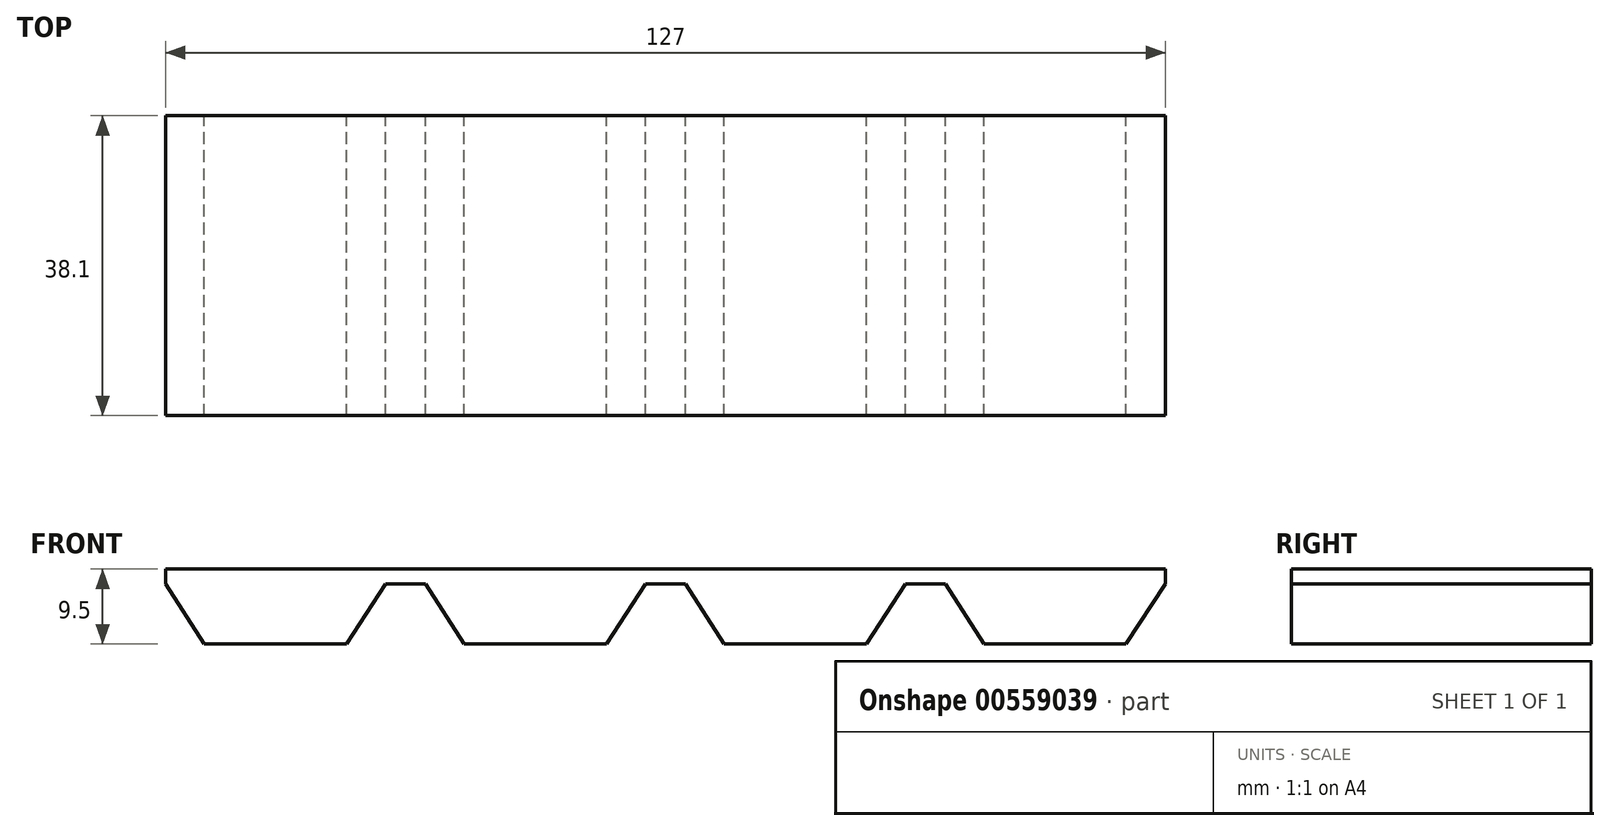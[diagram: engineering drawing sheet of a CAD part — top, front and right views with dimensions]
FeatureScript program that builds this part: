
annotation { "Feature Type Name" : "Feature", "Feature Type Description" : "" }
export const myFeature = defineFeature(function(context is Context, id is Id, definition is map)
    precondition{}
    {
        {
            var Q0;
            Q0=qCreatedBy(makeId("Front.planeOp"),FACE);
            var sketch = newSketch(context, id + "F0", { "sketchPlane" : qUnion([Q0])});
            skLineSegment(sketch, "E0", {"start": v(-63.5, 25.4) * mm, "end": v(63.5, 25.4) * mm});
            skLineSegment(sketch, "E1", {"start": v(-63.5, 25.4) * mm, "end": v(-58.6, 17.78) * mm});
            skLineSegment(sketch, "E2", {"start": v(-58.6, 17.78) * mm, "end": v(-40.55, 17.78) * mm});
            skLineSegment(sketch, "E3.MirrorCS", {"start": v(-35.56, 25.4) * mm, "end": v(-40.55, 17.78) * mm});
            skLineSegment(sketch, "E4.1.0.0", {"start": v(-2.54, 25.4) * mm, "end": v(-7.53, 17.78) * mm});
            skLineSegment(sketch, "E4.1.0.1", {"start": v(-25.58, 17.78) * mm, "end": v(-7.53, 17.78) * mm});
            skLineSegment(sketch, "E4.1.0.2", {"start": v(-30.48, 25.4) * mm, "end": v(-25.58, 17.78) * mm});
            skLineSegment(sketch, "E4.2.0.0", {"start": v(30.48, 25.4) * mm, "end": v(25.5, 17.78) * mm});
            skLineSegment(sketch, "E4.2.0.1", {"start": v(7.44, 17.78) * mm, "end": v(25.5, 17.78) * mm});
            skLineSegment(sketch, "E4.2.0.2", {"start": v(2.54, 25.4) * mm, "end": v(7.44, 17.78) * mm});
            skLineSegment(sketch, "E4.3.0.0", {"start": v(63.5, 25.4) * mm, "end": v(58.51, 17.78) * mm});
            skLineSegment(sketch, "E4.3.0.1", {"start": v(40.46, 17.78) * mm, "end": v(58.51, 17.78) * mm});
            skLineSegment(sketch, "E4.3.0.2", {"start": v(35.56, 25.4) * mm, "end": v(40.46, 17.78) * mm});
            skLineSegment(sketch, "E4.direction1", {"start": v(-58.6, 17.78) * mm, "end": v(-25.58, 17.78) * mm, "construction": true});
            skLineSegment(sketch, "E5", {"start": v(-63.5, 25.4) * mm, "end": v(-63.5, 27.28) * mm});
            skLineSegment(sketch, "E6", {"start": v(-63.5, 27.28) * mm, "end": v(63.48, 27.28) * mm});
            skLineSegment(sketch, "E7", {"start": v(63.48, 27.28) * mm, "end": v(63.5, 25.4) * mm});
            skSolve(sketch);
        }
        {
            var Q0;
            {var subQ0=sQuery(id+"F0.wireOp",EDGE,"E1");Q0=makeQuery(id+"F0.imprint","IMPRINT",FACE,{"disambiguationData":[TD([[makeQuery(id+"F0.imprint","IMPRINT",EDGE,{"derivedFrom":subQ0}),1.0]])]});}
            var Q1;
            {var subQ0=sQuery(id+"F0.wireOp",EDGE,"E4.1.0.0");Q1=makeQuery(id+"F0.imprint","IMPRINT",FACE,{"disambiguationData":[TD([[makeQuery(id+"F0.imprint","IMPRINT",EDGE,{"derivedFrom":subQ0}),-1.0]])]});}
            var Q2;
            {var subQ0=sQuery(id+"F0.wireOp",EDGE,"E4.2.0.0");Q2=makeQuery(id+"F0.imprint","IMPRINT",FACE,{"disambiguationData":[TD([[makeQuery(id+"F0.imprint","IMPRINT",EDGE,{"derivedFrom":subQ0}),-1.0]])]});}
            var Q3;
            {var subQ0=sQuery(id+"F0.wireOp",EDGE,"E4.3.0.0");Q3=makeQuery(id+"F0.imprint","IMPRINT",FACE,{"disambiguationData":[TD([[makeQuery(id+"F0.imprint","IMPRINT",EDGE,{"derivedFrom":subQ0}),-1.0]])]});}
            var Q4;
            {var subQ5=sQuery(id+"F0.wireOp",EDGE,"E5");Q4=makeQuery(id+"F0.imprint","IMPRINT",FACE,{"disambiguationData":[TD([[makeQuery(id+"F0.imprint","IMPRINT",EDGE,{"derivedFrom":subQ5}),-1.0]])]});}
            extrude(context, id + "F1", {"entities" : qUnion([Q0, Q1, Q2, Q3, Q4]), "depth" : 38.1 * mm, "offsetDistance" : 25.4 * mm});
        }
    });
